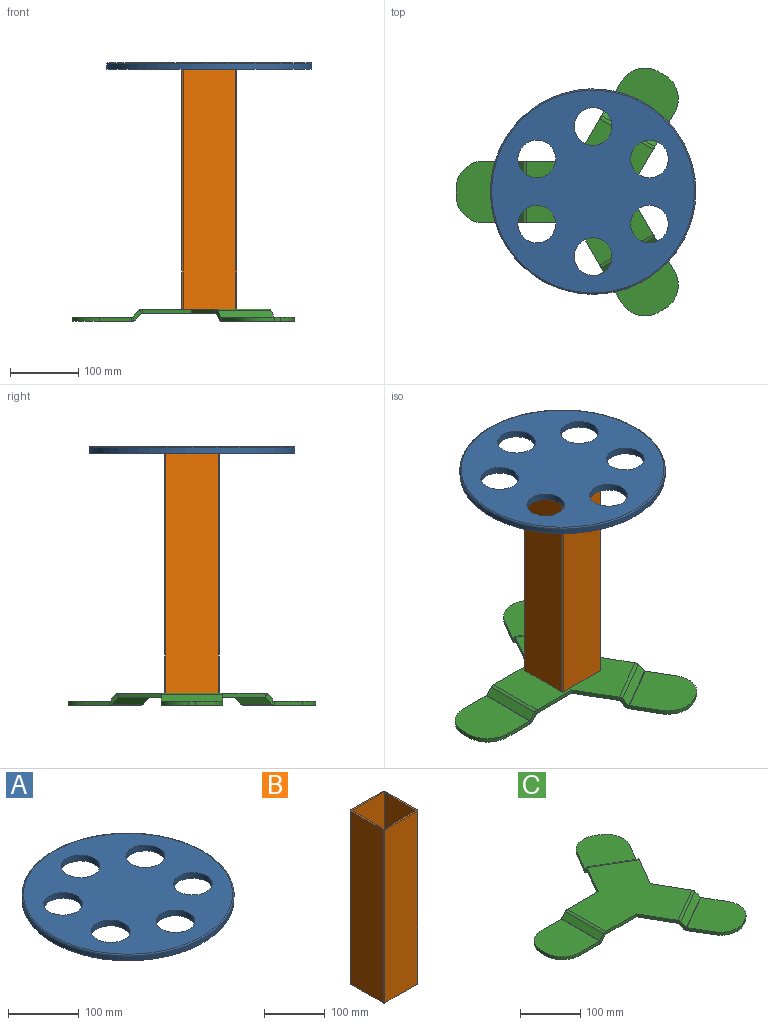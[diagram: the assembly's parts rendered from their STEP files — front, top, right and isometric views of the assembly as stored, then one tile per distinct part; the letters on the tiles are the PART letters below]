
ASSEMBLY  parts=3 mates=2
PART A: 10 faces, bbox 324.7x324.7x10 mm
  f0: cylinder r=150mm len=300mm, axis (0,0,-1), area 7539.8mm2, adj f2,f3
  f1: plane 296x296mm, normal (0,0,1), area 54558.5mm2, adj f3,f4,f5,f6,f7,f8,f9
  f2: plane 300x300mm, normal (0,0,-1), area 56430.9mm2, adj f0,f4,f5,f6,f7,f8,f9
  f3: torus R=148mm, axis (0,0,1), area 2946.5mm2, adj f0,f1
  f4: cylinder r=27.5mm len=55mm, axis (0,0,1), area 1727.9mm2, adj f1,f2
  f5: cylinder r=27.5mm len=55mm, axis (0,0,1), area 1727.9mm2, adj f1,f2
  f6: cylinder r=27.5mm len=55mm, axis (0,0,1), area 1727.9mm2, adj f1,f2
  f7: cylinder r=27.5mm len=55mm, axis (0,0,1), area 1727.9mm2, adj f1,f2
  f8: cylinder r=27.5mm len=55mm, axis (0,0,1), area 1727.9mm2, adj f1,f2
  f9: cylinder r=27.5mm len=55mm, axis (0,0,1), area 1727.9mm2, adj f1,f2
PART B: 14 faces, bbox 80x80x350 mm
  f0: plane 350x76mm, normal (1,0,0), area 26600mm2, adj f1,f11,f12,f13
  f1: cylinder r=2mm len=350mm, axis (0,0,-1), area 1099.6mm2, adj f0,f2,f12,f13
  f2: plane 350x76mm, normal (0,1,0), area 26600mm2, adj f1,f3,f12,f13
  f3: cylinder r=2mm len=350mm, axis (0,0,-1), area 1099.6mm2, adj f2,f4,f12,f13
  f4: plane 350x76mm, normal (-1,0,0), area 26600mm2, adj f3,f5,f12,f13
  f5: cylinder r=2mm len=350mm, axis (0,0,-1), area 1099.6mm2, adj f4,f6,f12,f13
  f6: plane 350x76mm, normal (0,-1,0), area 26600mm2, adj f5,f11,f12,f13
  f7: plane 350x74mm, normal (0,-1,0), area 25900mm2, adj f8,f10,f12,f13
  f8: plane 350x74mm, normal (-1,0,0), area 25900mm2, adj f7,f9,f12,f13
  f9: plane 350x74mm, normal (0,1,0), area 25900mm2, adj f8,f10,f12,f13
  f10: plane 350x74mm, normal (1,0,0), area 25900mm2, adj f7,f9,f12,f13
  f11: cylinder r=2mm len=350mm, axis (0,0,-1), area 1099.6mm2, adj f0,f6,f12,f13
  f12: plane 80x80mm, normal (0,0,1), area 920.6mm2, adj f0,f1,f2,f3,f4,f5,f6,f7
  f13: plane 80x80mm, normal (0,0,-1), area 920.6mm2, adj f0,f1,f2,f3,f4,f5,f6,f7
PART C: 65 faces, bbox 324.3x362.1x18 mm
  f0: plane 62.01x35.8mm, normal (0.87,0.5,0), area 429.6mm2, adj f1,f6,f7,f61
  f1: plane 62.01x35.8mm, normal (0.87,-0.5,0), area 429.6mm2, adj f0,f6,f7,f43
  f2: plane 62.01x35.8mm, normal (-0.87,0.5,0), area 429.6mm2, adj f3,f6,f7,f42
  f3: plane 71.61x6mm, normal (0,1,0), area 429.6mm2, adj f2,f6,f7,f24
  f4: plane 71.61x6mm, normal (0,-1,0), area 429.6mm2, adj f5,f6,f7,f23
  f5: plane 62.01x35.8mm, normal (-0.87,-0.5,0), area 429.6mm2, adj f4,f6,f7,f62
  f6: plane 214.02x185.35mm, normal (0,0,1), area 22840.8mm2, adj f0,f1,f2,f3,f4,f5,f25,f44
  f7: plane 214.02x185.35mm, normal (0,0,-1), area 22840.8mm2, adj f0,f1,f2,f3,f4,f5,f26,f45
  f8: plane 13.9x13.9mm, normal (0,1,0), area 81.9mm2, adj f10,f11,f20,f24
  f9: plane 13.9x13.9mm, normal (0,-1,0), area 81.9mm2, adj f10,f11,f19,f23
  f10: plane 90x9.66mm, normal (-0.71,0,0.71), area 1229.1mm2, adj f8,f9,f22,f25
  f11: plane 90x9.66mm, normal (0.71,0,-0.71), area 1229.1mm2, adj f8,f9,f21,f26
  f12: plane 47.1x6mm, normal (0,1,0), area 282.6mm2, adj f15,f16,f18,f20
  f13: plane 10x6mm, normal (-1,0,0), area 60mm2, adj f15,f16,f17,f18
  f14: plane 47.1x6mm, normal (0,-1,0), area 282.6mm2, adj f15,f16,f17,f19
  f15: plane 90x87.1mm, normal (0,0,1), area 7152.3mm2, adj f12,f13,f14,f17,f18,f22
  f16: plane 90x87.1mm, normal (0,0,-1), area 7152.3mm2, adj f12,f13,f14,f17,f18,f21
  f17: cylinder r=40mm len=40mm, axis (0,0,-1), area 377mm2, adj f13,f14,f15,f16
  f18: cylinder r=40mm len=40mm, axis (0,0,1), area 377mm2, adj f12,f13,f15,f16
  f19: plane 6.29x4.95mm, normal (0,-1,0), area 18.8mm2, adj f9,f14,f21,f22
  f20: plane 6.29x4.95mm, normal (0,1,0), area 18.8mm2, adj f8,f12,f21,f22
  f21: cylinder r=7mm len=90mm, axis (0,-1,0), area 494.8mm2, adj f11,f16,f19,f20
  f22: cylinder r=1mm len=90mm, axis (0,-1,0), area 70.7mm2, adj f10,f15,f19,f20
  f23: plane 6.29x4.95mm, normal (0,-1,0), area 18.8mm2, adj f4,f9,f25,f26
  f24: plane 6.29x4.95mm, normal (0,1,0), area 18.8mm2, adj f3,f8,f25,f26
  f25: cylinder r=7mm len=90mm, axis (0,-1,0), area 494.8mm2, adj f6,f10,f23,f24
  f26: cylinder r=1mm len=90mm, axis (0,-1,0), area 70.7mm2, adj f7,f11,f23,f24
  f27: plane 13.9x12.04mm, normal (0.87,-0.5,0), area 81.9mm2, adj f29,f30,f39,f43
  f28: plane 13.9x12.04mm, normal (-0.87,0.5,0), area 81.9mm2, adj f29,f30,f38,f42
  f29: plane 82.77x53.36mm, normal (0.35,0.61,0.71), area 1229.1mm2, adj f27,f28,f41,f44
  f30: plane 82.77x53.36mm, normal (-0.35,-0.61,-0.71), area 1229.1mm2, adj f27,f28,f40,f45
  f31: plane 40.79x23.55mm, normal (0.87,-0.5,0), area 282.6mm2, adj f34,f35,f36,f39
  f32: plane 8.66x6mm, normal (0.5,0.87,0), area 60mm2, adj f34,f35,f36,f37
  f33: plane 40.79x23.55mm, normal (-0.87,0.5,0), area 282.6mm2, adj f34,f35,f37,f38
  f34: plane 106.85x105.79mm, normal (0,0,1), area 7152.3mm2, adj f31,f32,f33,f36,f37,f41
  f35: plane 106.85x105.79mm, normal (0,0,-1), area 7152.3mm2, adj f31,f32,f33,f36,f37,f40
  f36: cylinder r=40mm len=54.64mm, axis (0,0,1), area 377mm2, adj f31,f32,f34,f35
  f37: cylinder r=40mm len=54.64mm, axis (0,0,-1), area 377mm2, adj f32,f33,f34,f35
  f38: plane 6.29x4.29mm, normal (-0.87,0.5,0), area 18.8mm2, adj f28,f33,f40,f41
  f39: plane 6.29x4.29mm, normal (0.87,-0.5,0), area 18.8mm2, adj f27,f31,f40,f41
  f40: cylinder r=7mm len=80.42mm, axis (-0.87,0.5,0), area 494.8mm2, adj f30,f35,f38,f39
  f41: cylinder r=1mm len=78.3mm, axis (-0.87,0.5,0), area 70.7mm2, adj f29,f34,f38,f39
  f42: plane 6.29x4.29mm, normal (-0.87,0.5,0), area 18.8mm2, adj f2,f28,f44,f45
  f43: plane 6.29x4.29mm, normal (0.87,-0.5,0), area 18.8mm2, adj f1,f27,f44,f45
  f44: cylinder r=7mm len=80.42mm, axis (-0.87,0.5,0), area 494.8mm2, adj f6,f29,f42,f43
  f45: cylinder r=1mm len=78.3mm, axis (-0.87,0.5,0), area 70.7mm2, adj f7,f30,f42,f43
  f46: plane 13.9x12.04mm, normal (-0.87,-0.5,0), area 81.9mm2, adj f48,f49,f58,f62
  f47: plane 13.9x12.04mm, normal (0.87,0.5,0), area 81.9mm2, adj f48,f49,f57,f61
  f48: plane 82.77x53.36mm, normal (0.35,-0.61,0.71), area 1229.1mm2, adj f46,f47,f60,f63
  f49: plane 82.77x53.36mm, normal (-0.35,0.61,-0.71), area 1229.1mm2, adj f46,f47,f59,f64
  f50: plane 40.79x23.55mm, normal (-0.87,-0.5,0), area 282.6mm2, adj f53,f54,f56,f58
  f51: plane 8.66x6mm, normal (0.5,-0.87,0), area 60mm2, adj f53,f54,f55,f56
  f52: plane 40.79x23.55mm, normal (0.87,0.5,0), area 282.6mm2, adj f53,f54,f55,f57
  f53: plane 106.85x105.79mm, normal (0,0,1), area 7152.3mm2, adj f50,f51,f52,f55,f56,f60
  f54: plane 106.85x105.79mm, normal (0,0,-1), area 7152.3mm2, adj f50,f51,f52,f55,f56,f59
  f55: cylinder r=40mm len=54.64mm, axis (0,0,-1), area 377mm2, adj f51,f52,f53,f54
  f56: cylinder r=40mm len=54.64mm, axis (0,0,1), area 377mm2, adj f50,f51,f53,f54
  f57: plane 6.29x4.29mm, normal (0.87,0.5,0), area 18.8mm2, adj f47,f52,f59,f60
  f58: plane 6.29x4.29mm, normal (-0.87,-0.5,0), area 18.8mm2, adj f46,f50,f59,f60
  f59: cylinder r=7mm len=80.42mm, axis (0.87,0.5,0), area 494.8mm2, adj f49,f54,f57,f58
  f60: cylinder r=1mm len=78.3mm, axis (0.87,0.5,0), area 70.7mm2, adj f48,f53,f57,f58
  f61: plane 6.29x4.29mm, normal (0.87,0.5,0), area 18.8mm2, adj f0,f47,f63,f64
  f62: plane 6.29x4.29mm, normal (-0.87,-0.5,0), area 18.8mm2, adj f5,f46,f63,f64
  f63: cylinder r=7mm len=80.42mm, axis (0.87,0.5,0), area 494.8mm2, adj f6,f48,f61,f62
  f64: cylinder r=1mm len=78.3mm, axis (0.87,0.5,0), area 70.7mm2, adj f7,f49,f61,f62
PLACE A t=(0,0,350)mm
PLACE B at identity
PLACE C t=(0,45,-6)mm
MATE fastened B.f13 <-> C.f6  axis (0,0,-1) through (0,0,0)mm
MATE fastened A.f0 <-> B.f12  axis (0,0,-1) through (0,0,350)mm
